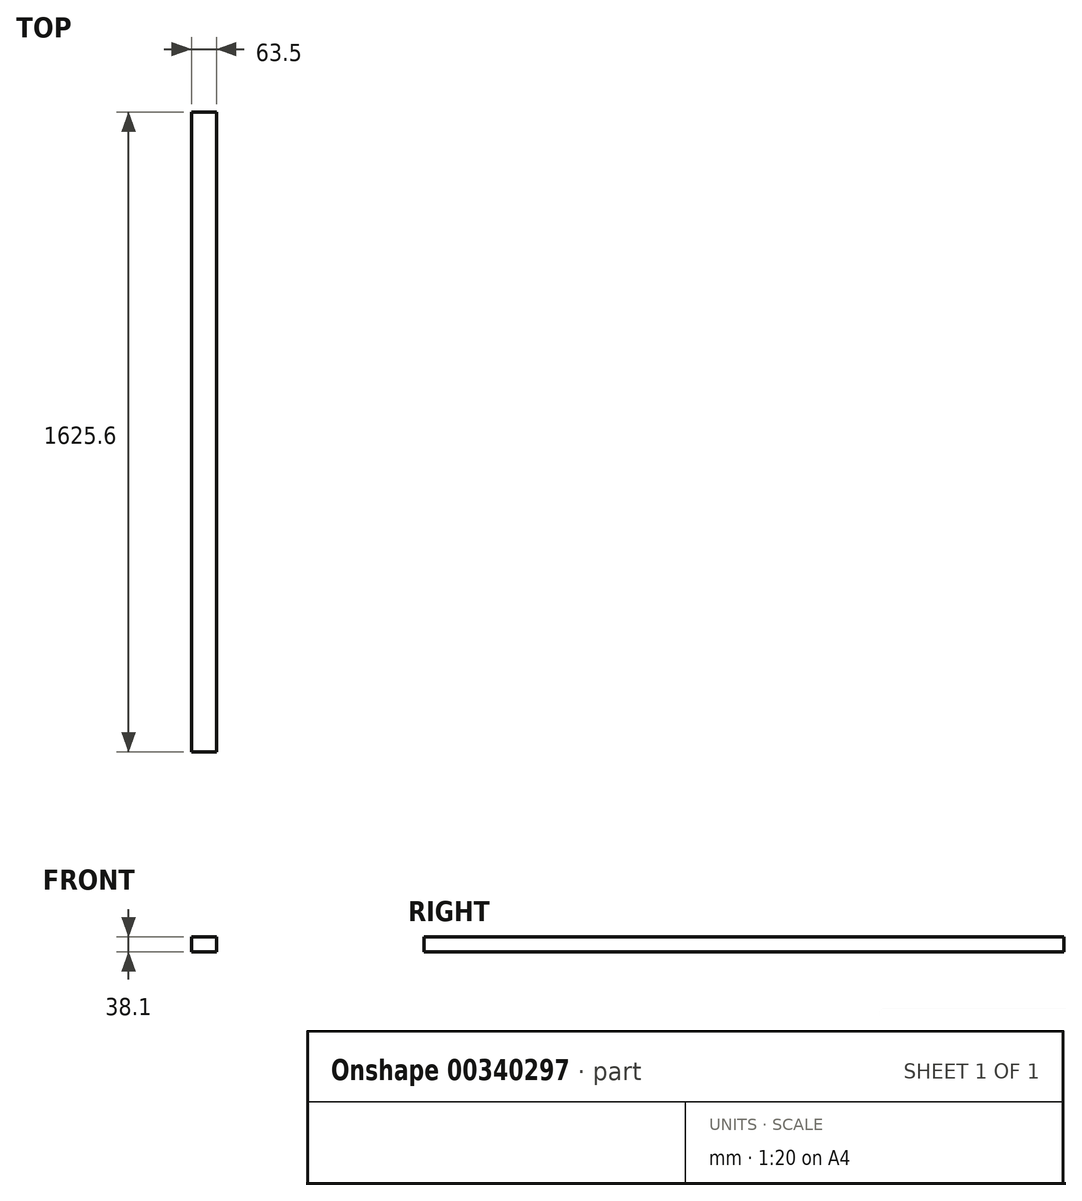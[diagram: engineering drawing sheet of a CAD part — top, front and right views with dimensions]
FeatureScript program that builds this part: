
annotation { "Feature Type Name" : "Feature", "Feature Type Description" : "" }
export const myFeature = defineFeature(function(context is Context, id is Id, definition is map)
    precondition{}
    {
        {
            var Q0;
            Q0=qCreatedBy(makeId("Front.planeOp"),FACE);
            var sketch = newSketch(context, id + "F0", { "sketchPlane" : qUnion([Q0])});
            skLineSegment(sketch, "E0.bottom", {"start": v(35.64, -16.66) * mm, "end": v(-27.86, -16.66) * mm});
            skLineSegment(sketch, "E0.top", {"start": v(35.64, 21.44) * mm, "end": v(-27.86, 21.44) * mm});
            skLineSegment(sketch, "E0.left", {"start": v(35.64, -16.66) * mm, "end": v(35.64, 21.44) * mm});
            skLineSegment(sketch, "E0.right", {"start": v(-27.86, -16.66) * mm, "end": v(-27.86, 21.44) * mm});
            skPoint(sketch, "E0.middle", {"position": v(3.9, 2.4) * mm});
            skSolve(sketch);
        }
        {
            var Q0;
            Q0 = qSketchRegion(id + "F0", true);
            extrude(context, id + "F1", {"entities" : qUnion([Q0]), "depth" : 1625.6 * mm});
        }
    });
